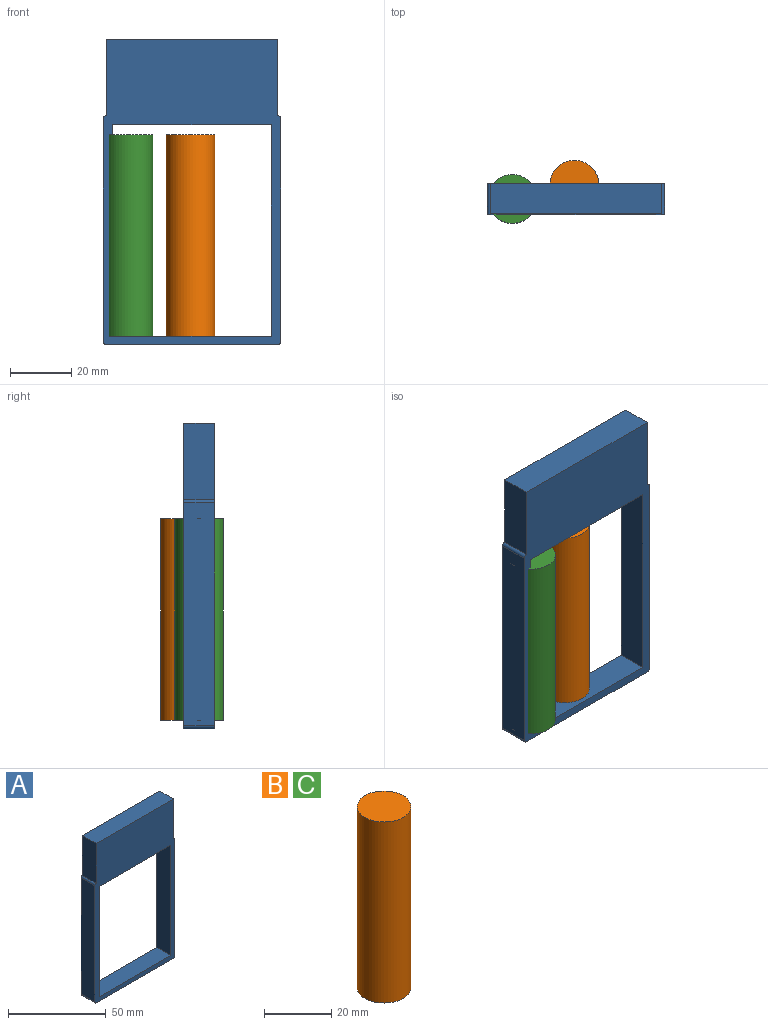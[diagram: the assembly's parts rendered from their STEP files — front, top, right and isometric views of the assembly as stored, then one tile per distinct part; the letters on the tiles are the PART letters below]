
ASSEMBLY  parts=3 mates=2
PART A: 16 faces, bbox 58x10x100 mm
  f0: cylinder r=1mm len=10mm, axis (0,1,0), area 15.7mm2, adj f1,f11,f12,f13
  f1: plane 73x10mm, normal (-1,0,0), area 730mm2, adj f0,f2,f11,f12
  f2: cylinder r=1mm len=10mm, axis (0,1,0), area 15.7mm2, adj f1,f3,f11,f12
  f3: plane 56x10mm, normal (0,0,-1), area 560mm2, adj f2,f4,f11,f12
  f4: cylinder r=1mm len=10mm, axis (0,1,0), area 15.7mm2, adj f3,f5,f11,f12
  f5: plane 73x10mm, normal (1,0,0), area 730mm2, adj f4,f10,f11,f12
  f6: plane 69.25x10mm, normal (1,0,0), area 692.5mm2, adj f7,f9,f11,f12
  f7: plane 52x10mm, normal (0,0,-1), area 520mm2, adj f6,f8,f11,f12
  f8: plane 69.25x10mm, normal (-1,0,0), area 692.5mm2, adj f7,f9,f11,f12
  f9: plane 52x10mm, normal (0,0,1), area 520mm2, adj f6,f8,f11,f12
  f10: cylinder r=1mm len=10mm, axis (0,1,0), area 15.7mm2, adj f5,f11,f12,f14
  f11: plane 100x58mm, normal (0,-1,0), area 2148.1mm2, adj f0,f1,f2,f3,f4,f5,f6,f7
  f12: plane 100x58mm, normal (0,1,0), area 2148.1mm2, adj f0,f1,f2,f3,f4,f5,f6,f7
  f13: plane 25x10mm, normal (-1,0,0), area 250mm2, adj f0,f11,f12,f15
  f14: plane 25x10mm, normal (1,0,0), area 250mm2, adj f10,f11,f12,f15
  f15: plane 56x10mm, normal (0,0,1), area 560mm2, adj f11,f12,f13,f14
PART B: 3 faces, bbox 16x16x66 mm
  f0: cylinder r=8mm len=66mm, axis (0,0,-1), area 3317.5mm2, adj f1,f2
  f1: plane 16x16mm, normal (0,0,1), area 201.1mm2, adj f0
  f2: plane 16x16mm, normal (0,0,-1), area 201.1mm2, adj f0
PART C: same geometry as B
PLACE A t=(12.62,14.14,8.73)mm
PLACE B t=(12.09,18.77,6.98)mm
PLACE C t=(-8.21,14.14,6.98)mm
MATE pin_slot C.f0 <-> A.f9  axis (0,0,-1) through (-8.21,14.14,-26.02)mm
MATE planar B.f0 <-> A.f9  axis (0,0,-1) through (12.09,18.77,-26.02)mm
